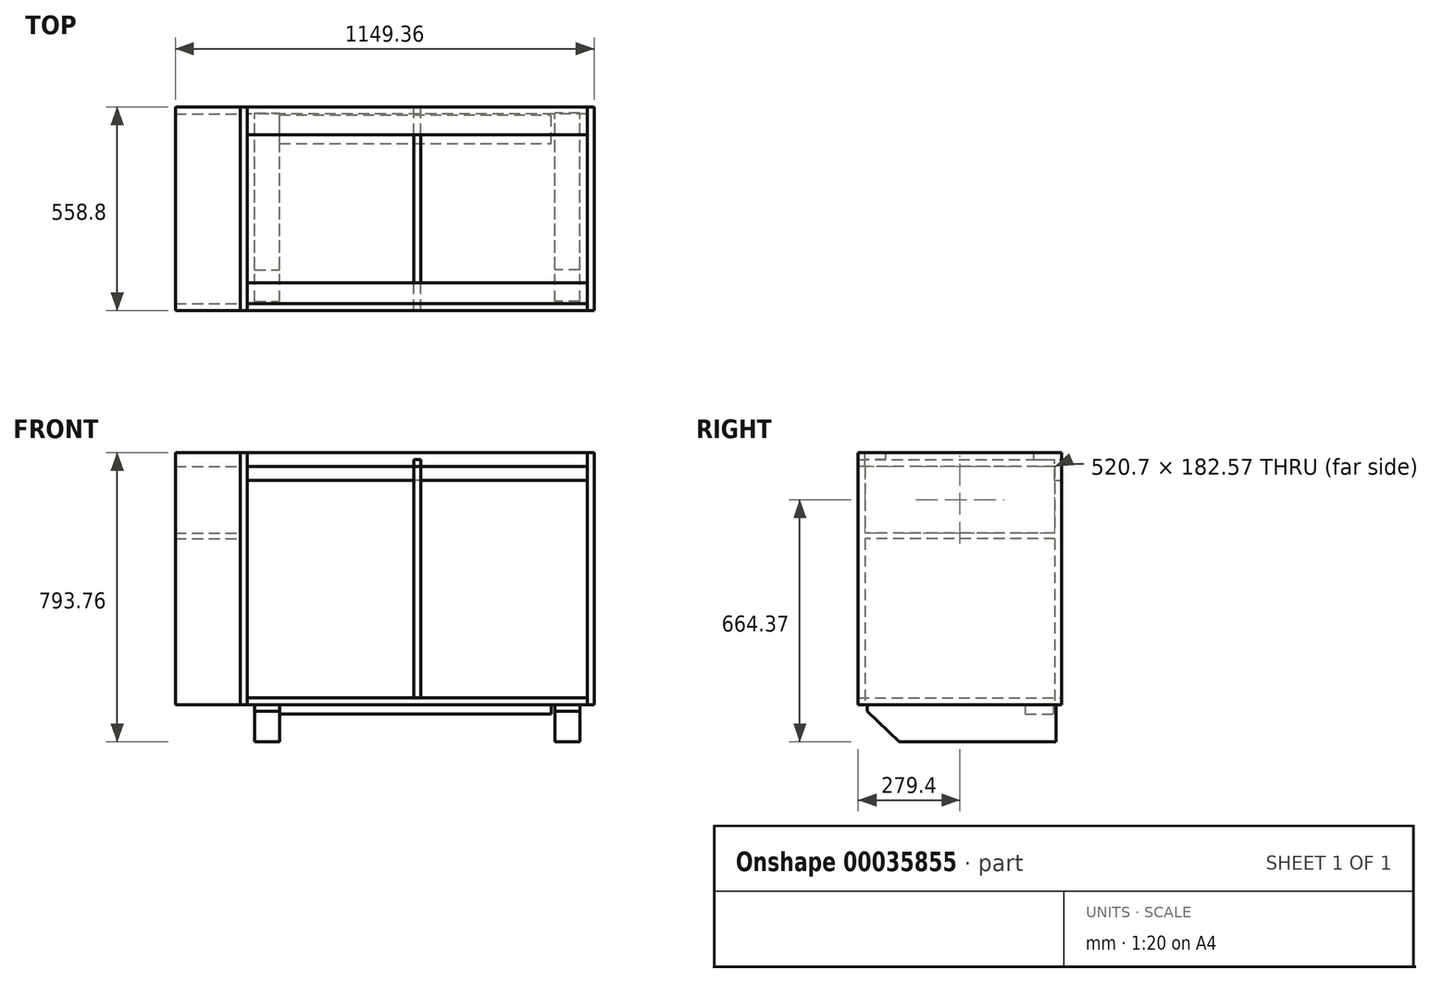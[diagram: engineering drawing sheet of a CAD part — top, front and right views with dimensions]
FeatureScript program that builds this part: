
annotation { "Feature Type Name" : "Feature", "Feature Type Description" : "" }
export const myFeature = defineFeature(function(context is Context, id is Id, definition is map)
    precondition{}
    {
        {
            var Q0;
            Q0=qCreatedBy(makeId("Front.planeOp"),FACE);
            var sketch = newSketch(context, id + "F0", { "sketchPlane" : qUnion([Q0])});
            skLineSegment(sketch, "E0.bottom", {"start": v(-485.77, 346.07) * mm, "end": v(485.78, 346.07) * mm, "construction": true});
            skLineSegment(sketch, "E0.top", {"start": v(-485.78, -346.08) * mm, "end": v(485.77, -346.08) * mm, "construction": true});
            skLineSegment(sketch, "E0.left", {"start": v(-485.78, 346.08) * mm, "end": v(-485.78, -346.07) * mm, "construction": true});
            skLineSegment(sketch, "E0.right", {"start": v(485.78, 346.07) * mm, "end": v(485.78, -346.08) * mm, "construction": true});
            skPoint(sketch, "E0.middle", {"position": v(0, 0) * mm});
            skLineSegment(sketch, "E1.bottom", {"start": v(-485.77, 346.07) * mm, "end": v(-466.73, 346.07) * mm});
            skLineSegment(sketch, "E1.top", {"start": v(-485.77, -346.08) * mm, "end": v(-466.73, -346.08) * mm});
            skLineSegment(sketch, "E1.left", {"start": v(-485.77, 346.08) * mm, "end": v(-485.77, -346.08) * mm});
            skLineSegment(sketch, "E1.right", {"start": v(-466.73, 346.08) * mm, "end": v(-466.73, -346.08) * mm});
            skLineSegment(sketch, "E2.MirrorCS", {"start": v(485.77, 346.08) * mm, "end": v(485.77, -346.08) * mm});
            skLineSegment(sketch, "E3.MirrorCS", {"start": v(466.73, 346.08) * mm, "end": v(466.73, -346.08) * mm});
            skLineSegment(sketch, "E4.MirrorCS", {"start": v(485.77, 346.07) * mm, "end": v(466.73, 346.07) * mm});
            skLineSegment(sketch, "E5.MirrorCS", {"start": v(485.77, -346.08) * mm, "end": v(466.73, -346.08) * mm});
            skLineSegment(sketch, "E6.bottom", {"start": v(-466.73, -346.08) * mm, "end": v(466.73, -346.08) * mm});
            skLineSegment(sketch, "E6.top", {"start": v(-466.73, -327.02) * mm, "end": v(466.73, -327.02) * mm});
            skLineSegment(sketch, "E6.left", {"start": v(-466.73, -346.08) * mm, "end": v(-466.73, -327.02) * mm});
            skLineSegment(sketch, "E6.right", {"start": v(466.73, -346.08) * mm, "end": v(466.73, -327.02) * mm});
            skLineSegment(sketch, "E7.MirrorCS", {"start": v(-466.73, 346.08) * mm, "end": v(466.73, 346.08) * mm});
            skLineSegment(sketch, "E8.MirrorCS", {"start": v(-466.73, 327.02) * mm, "end": v(466.73, 327.02) * mm});
            skLineSegment(sketch, "E9.bottom", {"start": v(-9.53, -327.02) * mm, "end": v(9.53, -327.02) * mm});
            skLineSegment(sketch, "E9.top", {"start": v(-9.53, 327.02) * mm, "end": v(9.53, 327.02) * mm});
            skLineSegment(sketch, "E9.left", {"start": v(-9.53, -327.03) * mm, "end": v(-9.53, 327.03) * mm});
            skLineSegment(sketch, "E9.right", {"start": v(9.53, -327.03) * mm, "end": v(9.53, 327.03) * mm});
            skSolve(sketch);
        }
        {
            var Q0;
            {var subQ4=sQuery(id+"F0.wireOp",EDGE,"E1.bottom");Q0=makeQuery(id+"F0.imprint","IMPRINT",FACE,{"disambiguationData":[TD([[makeQuery(id+"F0.imprint","IMPRINT",EDGE,{"derivedFrom":subQ4}),-1.0]])]});}
            extrude(context, id + "F1", {"entities" : qUnion([Q0]), "depth" : 558.8 * mm});
        }
        {
            var Q0;
            {var subQ0=sQuery(id+"F0.wireOp",EDGE,"E6.bottom");Q0=makeQuery(id+"F0.imprint","IMPRINT",FACE,{"disambiguationData":[TD([[makeQuery(id+"F0.imprint","IMPRINT",EDGE,{"derivedFrom":subQ0}),1.0]])]});}
            extrude(context, id + "F2", {"entities" : qUnion([Q0]), "depth" : 558.8 * mm});
        }
        {
            var Q0;
            Q0=makeQuery(id+"F1.opExtrude","SWEPT_BODY",BODY,{"disambiguationData":[OSD([sQuery(id+"F0.wireOp",EDGE,"E1.bottom"),sQuery(id+"F0.wireOp",EDGE,"E1.top"),sQuery(id+"F0.wireOp",EDGE,"E1.left"),sQuery(id+"F0.wireOp",EDGE,"E1.right")])]});
            var Q1;
            Q1=qCreatedBy(makeId("Right.planeOp"),FACE);
            mirror(context, id + "F3", {"entities" : qUnion([Q0]), "mirrorPlane" : qUnion([Q1])});
        }
        {
            var Q0;
            {var subQ2=sQuery(id+"F0.wireOp",EDGE,"E9.left");Q0=makeQuery(id+"F0.imprint","IMPRINT",FACE,{"disambiguationData":[TD([[makeQuery(id+"F0.imprint","IMPRINT",EDGE,{"derivedFrom":subQ2}),-1.0]])]});}
            extrude(context, id + "F4", {"entities" : qUnion([Q0]), "depth" : 558.8 * mm});
        }
        {
            var Q0;
            Q0=makeQuery(id+"F1.opExtrude","SWEPT_FACE",FACE,{"disambiguationData":[OSD([sQuery(id+"F0.wireOp",EDGE,"E1.right")])]});
            var sketch = newSketch(context, id + "F5", { "sketchPlane" : qUnion([Q0])});
            skLineSegment(sketch, "E10.bottom", {"start": v(-558.8, 346.08) * mm, "end": v(-539.75, 346.08) * mm});
            skLineSegment(sketch, "E10.top", {"start": v(-558.8, 307.98) * mm, "end": v(-539.75, 307.98) * mm});
            skLineSegment(sketch, "E10.left", {"start": v(-558.8, 346.08) * mm, "end": v(-558.8, 307.98) * mm});
            skLineSegment(sketch, "E10.right", {"start": v(-539.75, 346.08) * mm, "end": v(-539.75, 307.98) * mm});
            skLineSegment(sketch, "E11.bottom", {"start": v(-539.75, 346.08) * mm, "end": v(-482.6, 346.08) * mm});
            skLineSegment(sketch, "E11.top", {"start": v(-539.75, 327.03) * mm, "end": v(-482.6, 327.03) * mm});
            skLineSegment(sketch, "E11.left", {"start": v(-539.75, 346.08) * mm, "end": v(-539.75, 327.03) * mm});
            skLineSegment(sketch, "E11.right", {"start": v(-482.6, 346.08) * mm, "end": v(-482.6, 327.03) * mm});
            skLineSegment(sketch, "E12.bottom", {"start": v(0, 346.08) * mm, "end": v(-76.2, 346.08) * mm});
            skLineSegment(sketch, "E12.top", {"start": v(0, 327.02) * mm, "end": v(-76.2, 327.02) * mm});
            skLineSegment(sketch, "E12.left", {"start": v(0, 346.08) * mm, "end": v(0, 327.02) * mm});
            skLineSegment(sketch, "E12.right", {"start": v(-76.2, 346.08) * mm, "end": v(-76.2, 327.02) * mm});
            skLineSegment(sketch, "E13.bottom", {"start": v(0, 327.02) * mm, "end": v(-19.05, 327.02) * mm});
            skLineSegment(sketch, "E13.top", {"start": v(0, 269.88) * mm, "end": v(-19.05, 269.88) * mm});
            skLineSegment(sketch, "E13.left", {"start": v(0, 327.02) * mm, "end": v(0, 269.88) * mm});
            skLineSegment(sketch, "E13.right", {"start": v(-19.05, 327.03) * mm, "end": v(-19.05, 269.88) * mm});
            skSolve(sketch);
        }
        {
            var Q0;
            {var subQ3=sQuery(id+"F5.wireOp",EDGE,"E10.bottom");Q0=makeQuery(id+"F5.imprint","IMPRINT",FACE,{"disambiguationData":[TD([[makeQuery(id+"F5.imprint","IMPRINT",EDGE,{"derivedFrom":subQ3}),-1.0]])]});}
            var Q1;
            Q1=makeQuery(id+"F3.opPattern","COPY",FACE,{"derivedFrom":makeQuery(id+"F1.opExtrude","SWEPT_FACE",FACE,{"disambiguationData":[OSD([sQuery(id+"F0.wireOp",EDGE,"E1.right")])]}),"instanceName":"1"});
            extrude(context, id + "F6", {"entities" : qUnion([Q0]), "endBound" : BoundingType.UP_TO_SURFACE, "endBoundEntityFace" : qUnion([Q1]), "depth" : 25.4 * mm});
        }
        {
            var Q0;
            {var subQ0=sQuery(id+"F5.wireOp",EDGE,"E11.bottom");Q0=makeQuery(id+"F5.imprint","IMPRINT",FACE,{"disambiguationData":[TD([[makeQuery(id+"F5.imprint","IMPRINT",EDGE,{"derivedFrom":subQ0}),-1.0]])]});}
            var Q1;
            Q1=makeQuery(id+"F5.imprint","IMPRINT",FACE,{"disambiguationData":[TD([[makeQuery(id+"F5.imprint","IMPRINT",EDGE,{"derivedFrom":sQuery(id+"F5.wireOp",EDGE,"E12.bottom")}),-1.0]])]});
            var Q2;
            Q2=makeQuery(id+"F5.imprint","IMPRINT",FACE,{"disambiguationData":[TD([[makeQuery(id+"F5.imprint","IMPRINT",EDGE,{"derivedFrom":sQuery(id+"F5.wireOp",EDGE,"E13.top")}),-1.0]])]});
            var Q3;
            Q3=makeQuery(id+"F3.opPattern","COPY",FACE,{"derivedFrom":makeQuery(id+"F1.opExtrude","SWEPT_FACE",FACE,{"disambiguationData":[OSD([sQuery(id+"F0.wireOp",EDGE,"E1.right")])]}),"instanceName":"1"});
            extrude(context, id + "F7", {"entities" : qUnion([Q0, Q1, Q2]), "endBound" : BoundingType.UP_TO_SURFACE, "endBoundEntityFace" : qUnion([Q3]), "depth" : 25.4 * mm});
        }
        {
            var Q0;
            Q0=makeQuery(id+"F1.opExtrude","SWEPT_FACE",FACE,{"disambiguationData":[OSD([sQuery(id+"F0.wireOp",EDGE,"E1.left")])]});
            var sketch = newSketch(context, id + "F8", { "sketchPlane" : qUnion([Q0])});
            skLineSegment(sketch, "E14.bottom", {"start": v(0, 346.08) * mm, "end": v(19.05, 346.08) * mm});
            skLineSegment(sketch, "E14.top", {"start": v(0, -346.08) * mm, "end": v(19.05, -346.08) * mm});
            skLineSegment(sketch, "E14.left", {"start": v(0, 346.08) * mm, "end": v(0, -346.08) * mm});
            skLineSegment(sketch, "E14.right", {"start": v(19.05, 346.08) * mm, "end": v(19.05, -346.08) * mm});
            skLineSegment(sketch, "E15.bottom", {"start": v(558.8, 346.08) * mm, "end": v(539.75, 346.08) * mm});
            skLineSegment(sketch, "E15.top", {"start": v(558.8, -346.08) * mm, "end": v(539.75, -346.08) * mm});
            skLineSegment(sketch, "E15.left", {"start": v(558.8, 346.08) * mm, "end": v(558.8, -346.08) * mm});
            skLineSegment(sketch, "E15.right", {"start": v(539.75, 346.08) * mm, "end": v(539.75, -346.08) * mm});
            skLineSegment(sketch, "E16.bottom", {"start": v(19.05, 346.08) * mm, "end": v(539.75, 346.08) * mm});
            skLineSegment(sketch, "E16.top", {"start": v(19.05, 307.98) * mm, "end": v(539.75, 307.98) * mm});
            skLineSegment(sketch, "E16.left", {"start": v(19.05, 346.08) * mm, "end": v(19.05, 307.98) * mm});
            skLineSegment(sketch, "E16.right", {"start": v(539.75, 346.08) * mm, "end": v(539.75, 307.98) * mm});
            skLineSegment(sketch, "E17.bottom", {"start": v(19.05, 125.4) * mm, "end": v(539.75, 125.4) * mm});
            skLineSegment(sketch, "E17.top", {"start": v(19.05, 109.38) * mm, "end": v(539.75, 109.38) * mm});
            skLineSegment(sketch, "E17.left", {"start": v(19.05, 125.4) * mm, "end": v(19.05, 109.38) * mm});
            skLineSegment(sketch, "E17.right", {"start": v(539.75, 125.4) * mm, "end": v(539.75, 109.38) * mm});
            skSolve(sketch);
        }
        {
            var Q0;
            {var subQ3=sQuery(id+"F8.wireOp",EDGE,"E15.bottom");Q0=makeQuery(id+"F8.imprint","IMPRINT",FACE,{"disambiguationData":[TD([[makeQuery(id+"F8.imprint","IMPRINT",EDGE,{"derivedFrom":subQ3}),1.0]])]});}
            var Q1;
            {var subQ0=sQuery(id+"F8.wireOp",EDGE,"E16.bottom");Q1=makeQuery(id+"F8.imprint","IMPRINT",FACE,{"disambiguationData":[TD([[makeQuery(id+"F8.imprint","IMPRINT",EDGE,{"derivedFrom":subQ0}),1.0]])]});}
            var Q2;
            {var subQ2=sQuery(id+"F8.wireOp",EDGE,"E17.bottom");Q2=makeQuery(id+"F8.imprint","IMPRINT",FACE,{"disambiguationData":[TD([[makeQuery(id+"F8.imprint","IMPRINT",EDGE,{"derivedFrom":subQ2}),-1.0]])]});}
            var Q3;
            {var subQ3=sQuery(id+"F8.wireOp",EDGE,"E14.bottom");Q3=makeQuery(id+"F8.imprint","IMPRINT",FACE,{"disambiguationData":[TD([[makeQuery(id+"F8.imprint","IMPRINT",EDGE,{"derivedFrom":subQ3}),1.0]])]});}
            extrude(context, id + "F9", {"entities" : qUnion([Q0, Q1, Q2, Q3]), "depth" : 177.8 * mm});
        }
        {
            var Q0;
            Q0=makeQuery(id+"F2.opExtrude","SWEPT_FACE",FACE,{"disambiguationData":[OSD([sQuery(id+"F0.wireOp",EDGE,"E6.bottom")])]});
            var sketch = newSketch(context, id + "F10", { "sketchPlane" : qUnion([Q0])});
            skLineSegment(sketch, "E18.bottom", {"start": v(-446.13, 534.03) * mm, "end": v(-378.04, 534.03) * mm});
            skLineSegment(sketch, "E18.top", {"start": v(-446.13, 16.26) * mm, "end": v(-378.04, 16.26) * mm});
            skLineSegment(sketch, "E18.left", {"start": v(-446.13, 534.03) * mm, "end": v(-446.13, 16.26) * mm});
            skLineSegment(sketch, "E18.right", {"start": v(-378.04, 534.03) * mm, "end": v(-378.04, 16.26) * mm});
            skLineSegment(sketch, "E19.bottom", {"start": v(-378.04, 99.95) * mm, "end": v(368.11, 99.95) * mm});
            skLineSegment(sketch, "E19.top", {"start": v(-378.04, 21.93) * mm, "end": v(368.11, 21.93) * mm});
            skLineSegment(sketch, "E19.left", {"start": v(-378.04, 99.95) * mm, "end": v(-378.04, 21.93) * mm});
            skLineSegment(sketch, "E19.right", {"start": v(368.11, 99.95) * mm, "end": v(368.11, 21.93) * mm});
            skSolve(sketch);
        }
        {
            var Q0;
            {var subQ0=sQuery(id+"F10.wireOp",EDGE,"E19.bottom");Q0=makeQuery(id+"F10.imprint","IMPRINT",FACE,{"disambiguationData":[TD([[makeQuery(id+"F10.imprint","IMPRINT",EDGE,{"derivedFrom":subQ0}),-1.0]])]});}
            extrude(context, id + "F11", {"entities" : qUnion([Q0]), "depth" : 25.4 * mm});
        }
        {
            var Q0;
            {var subQ1=sQuery(id+"F10.wireOp",EDGE,"E18.bottom");Q0=makeQuery(id+"F10.imprint","IMPRINT",FACE,{"disambiguationData":[TD([[makeQuery(id+"F10.imprint","IMPRINT",EDGE,{"derivedFrom":subQ1}),-1.0]])]});}
            extrude(context, id + "F12", {"entities" : qUnion([Q0]), "depth" : 101.6 * mm});
        }
        {
            var Q0;
            Q0=makeQuery(id+"F12.opExtrude","SWEPT_FACE",FACE,{"disambiguationData":[OSD([sQuery(id+"F10.wireOp",EDGE,"E18.right")])]});
            var sketch = newSketch(context, id + "F13", { "sketchPlane" : qUnion([Q0])});
            skLineSegment(sketch, "E20", {"start": v(-534.03, -363.43) * mm, "end": v(-446.67, -447.68) * mm});
            skSolve(sketch);
        }
        {
            var Q0;
            {var subQ0=sQuery(id+"F13.wireOp",EDGE,"E20");Q0=makeQuery(id+"F13.imprint","IMPRINT",FACE,{"disambiguationData":[TD([[makeQuery(id+"F13.imprint","IMPRINT",EDGE,{"derivedFrom":subQ0}),-1.0]])]});}
            extrude(context, id + "F14", {"entities" : qUnion([Q0]), "operationType" : NewBodyOperationType.REMOVE, "oppositeDirection" : true, "depth" : 101.6 * mm});
        }
        {
            var Q0;
            Q0=makeQuery(id+"F12.opExtrude","SWEPT_BODY",BODY,{"disambiguationData":[OSD([sQuery(id+"F10.wireOp",EDGE,"E18.bottom"),sQuery(id+"F10.wireOp",EDGE,"E18.top"),sQuery(id+"F10.wireOp",EDGE,"E18.left"),sQuery(id+"F10.wireOp",EDGE,"E18.right")])]});
            var Q1;
            Q1=qCreatedBy(makeId("Right.planeOp"),FACE);
            mirror(context, id + "F15", {"operationType" : NewBodyOperationType.ADD, "entities" : qUnion([Q0]), "mirrorPlane" : qUnion([Q1])});
        }
    });
